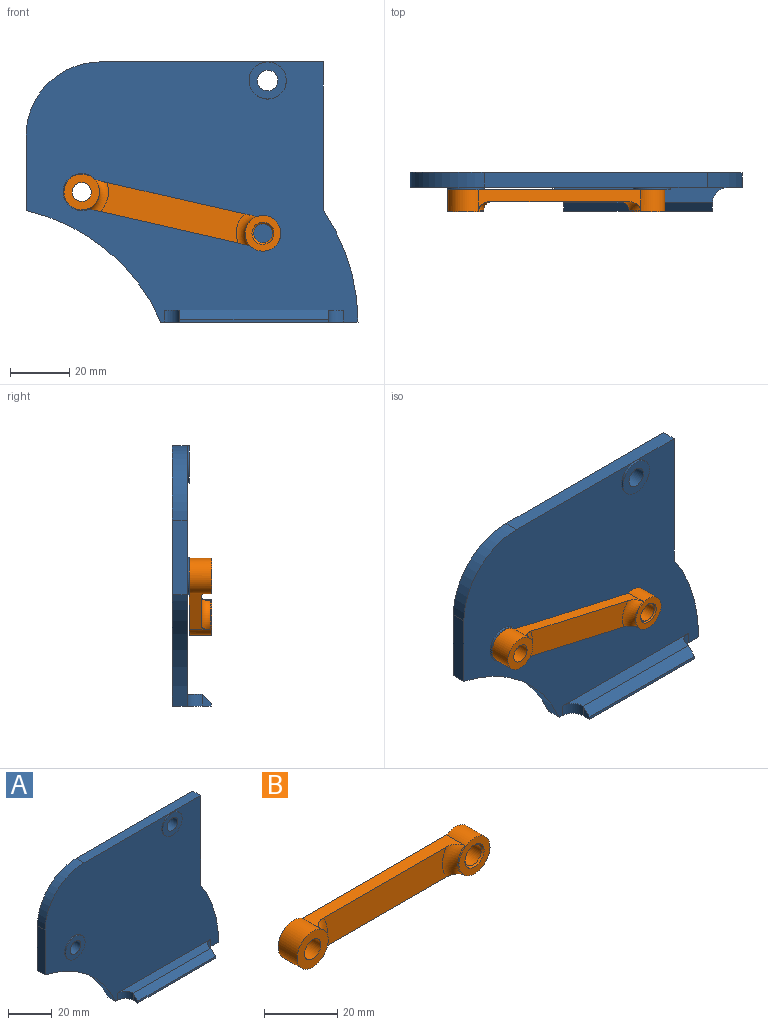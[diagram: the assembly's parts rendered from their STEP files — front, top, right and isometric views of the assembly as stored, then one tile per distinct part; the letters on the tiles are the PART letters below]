
ASSEMBLY  parts=2 mates=1
PART A: 22 faces, bbox 111.6x13x87.5 mm
  f0: plane 75x5mm, normal (0,0,1), area 375mm2, adj f7,f8,f9,f10
  f1: plane 25x5mm, normal (-1,0,0), area 125mm2, adj f2,f8,f9,f10
  f2: cylinder r=65mm len=45.38mm, axis (0,1,0), area 305.5mm2, adj f1,f3,f8,f9
  f3: plane 66.25x13mm, normal (0,0,-1), area 742mm2, adj f2,f4,f8,f9,f15,f16,f17,f19
  f4: cylinder r=66.25mm len=37.5mm, axis (0,1,0), area 199.3mm2, adj f3,f7,f8,f9
  f5: cylinder r=3.45mm len=6.91mm, axis (0,1,0), area 124mm2, adj f9,f12
  f6: cylinder r=3.45mm len=6.91mm, axis (0,1,0), area 124mm2, adj f9,f14
  f7: plane 50x5mm, normal (1,0,0), area 250mm2, adj f0,f4,f8,f9
  f8: plane 111.63x87.5mm, normal (0,-1,0), area 7296.2mm2, adj f0,f1,f2,f3,f4,f7,f10,f11
  f9: plane 111.63x87.5mm, normal (0,1,0), area 7706.6mm2, adj f0,f1,f2,f3,f4,f5,f6,f7
  f10: cylinder r=25mm len=25mm, axis (0,-1,0), area 196.3mm2, adj f0,f1,f8,f9
  f11: cylinder r=6.25mm len=12.5mm, axis (0,1,0), area 28.1mm2, adj f8,f12
  f12: plane 12.5x12.5mm, normal (0,-1,0), area 85.2mm2, adj f5,f11
  f13: cylinder r=6.25mm len=12.5mm, axis (0,1,0), area 28.1mm2, adj f8,f14
  f14: plane 12.5x12.5mm, normal (0,-1,0), area 85.2mm2, adj f6,f13
  f15: plane 4x3mm, normal (-1,0,0), area 7.5mm2, adj f3,f17,f19,f21
  f16: plane 4x3mm, normal (1,0,0), area 7.5mm2, adj f3,f17,f20,f21
  f17: plane 50x1mm, normal (0,-1,0), area 50mm2, adj f3,f15,f16,f21
  f18: plane 60x5mm, normal (0,0,1), area 260.7mm2, adj f8,f19,f20,f21
  f19: cylinder r=5mm len=5mm, axis (0,0,-1), area 31.4mm2, adj f3,f8,f15,f18
  f20: cylinder r=5mm len=5mm, axis (0,0,-1), area 31.4mm2, adj f3,f8,f16,f18
  f21: plane 50x3mm, normal (0,-0.71,0.71), area 212.1mm2, adj f15,f16,f17,f18
PART B: 13 faces, bbox 74.5x9.1x20.1 mm
  f0: plane 55.87x7mm, normal (0,0,1), area 229.5mm2, adj f4,f5,f8,f9,f10,f11
  f1: plane 55.87x7mm, normal (0,0,-1), area 229.5mm2, adj f4,f5,f8,f9,f10,f11
  f2: plane 12x12mm, normal (0,-1,0), area 80.9mm2, adj f5,f6
  f3: plane 12x12mm, normal (0,-1,0), area 70.1mm2, adj f4,f12
  f4: cylinder r=6mm len=12mm, axis (0,1,0), area 196.2mm2, adj f0,f1,f3,f8,f10
  f5: cylinder r=6mm len=12mm, axis (0,1,0), area 196.2mm2, adj f0,f1,f2,f8,f11
  f6: cylinder r=3.2mm len=7.4mm, axis (0,1,0), area 148.8mm2, adj f2,f8
  f7: cylinder r=3.2mm len=6.9mm, axis (0,1,0), area 138.7mm2, adj f8,f12
  f8: plane 74.5x12mm, normal (0,1,0), area 682.8mm2, adj f0,f1,f4,f5,f6,f7
  f9: plane 47.53x10mm, normal (0,-1,0), area 454.7mm2, adj f0,f1,f10,f11
  f10: torus R=9mm, axis (0,-1,0), area 52.9mm2, adj f0,f1,f4,f9
  f11: torus R=9mm, axis (0,-1,0), area 52.9mm2, adj f0,f1,f5,f9
  f12: cone r=3.2mm half-angle=45deg, axis (0,-1,0), area 15.3mm2, adj f3,f7
PLACE A t=(-5.79,-2.5,-12.94)mm fixed
PLACE B rot(axis=(0,1,0),12.8deg) t=(-68.29,-8.22,-12.94)mm
MATE revolute B.f5 <-> A.f11  axis (0,1,0) through (-68.29,-8.22,-12.94)mm
